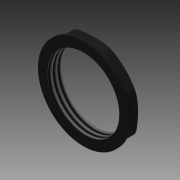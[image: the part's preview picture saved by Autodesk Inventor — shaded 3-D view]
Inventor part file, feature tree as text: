
AUTODESK INVENTOR PART (.ipt)
format: ipt  version: 2016 SP1 (Build 200210100, 210)  size: 116,736 bytes
history: native  units: mm
features: imported_body x1, thread x1
ambient origin geometry x8: Origin, YZ Plane, XZ Plane, XY Plane, X Axis, Y Axis, Z Axis, Center Point
bodies: Solid1 (feature_tree)
feature tree (2):
  imported_body  "Base1"
  thread  "Thread1"  [1 undecoded]
note: 1 required parameter value undecoded (feature->parameter linkage not recoverable at this tier; creation-order binding heuristic only, values carry confidence <= 0.55)
